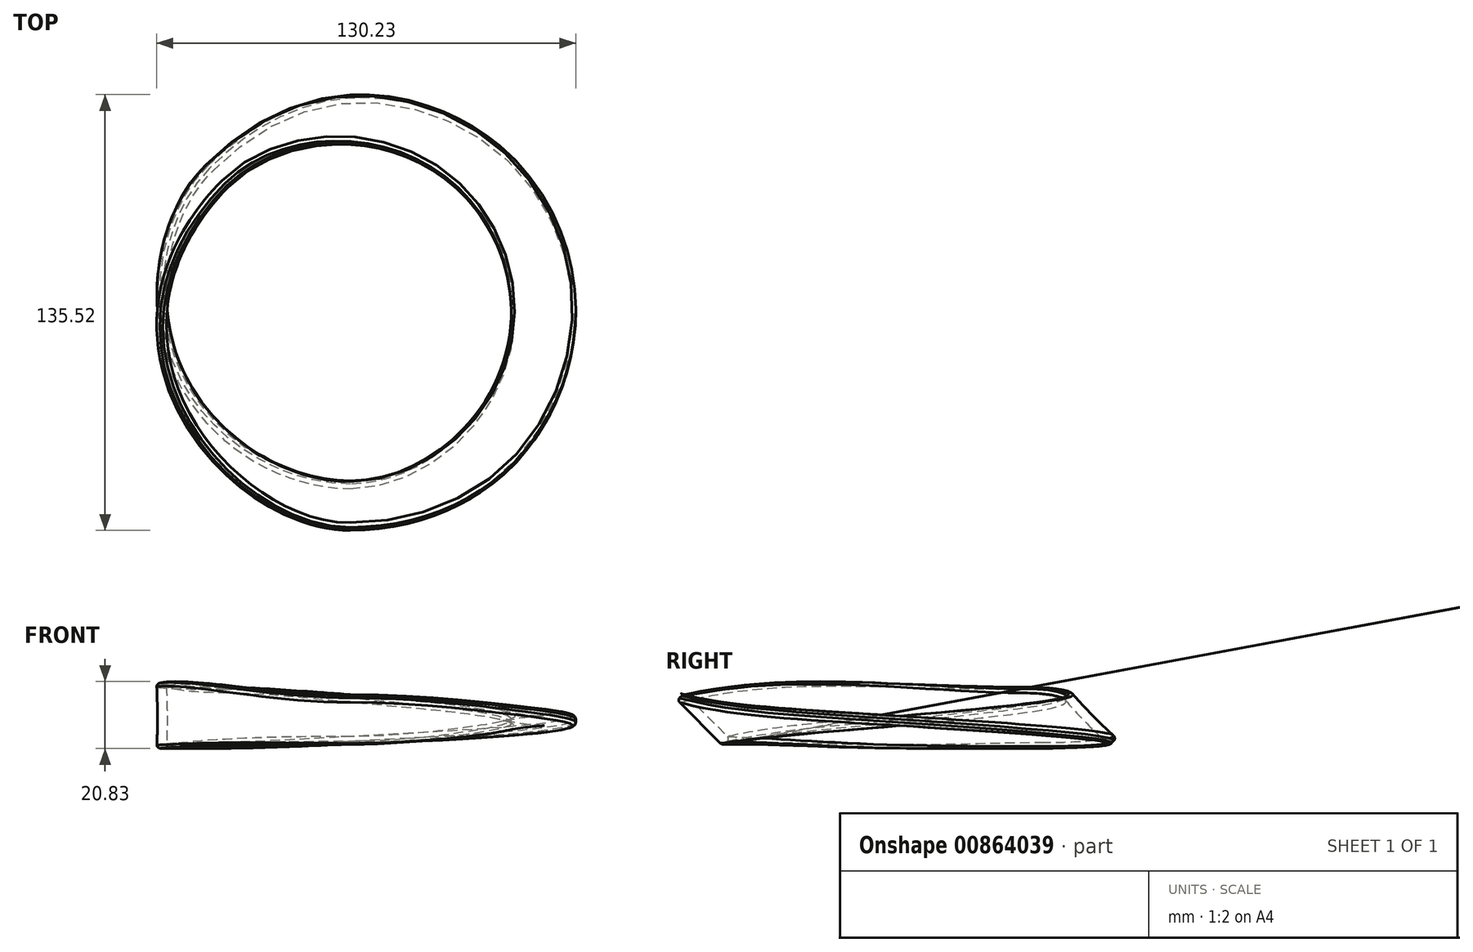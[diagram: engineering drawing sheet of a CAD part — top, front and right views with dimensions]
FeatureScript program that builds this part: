
annotation { "Feature Type Name" : "Feature", "Feature Type Description" : "" }
export const myFeature = defineFeature(function(context is Context, id is Id, definition is map)
    precondition{}
    {
        {
            var Q0;
            Q0=qCreatedBy(makeId("Front.planeOp"),FACE);
            var sketch = newSketch(context, id + "F0", { "sketchPlane" : qUnion([Q0])});
            skLineSegment(sketch, "E0", {"start": v(-60, 10) * mm, "end": v(-60, -10) * mm});
            skLineSegment(sketch, "E1", {"start": v(50, 0) * mm, "end": v(70, 0) * mm});
            skLineSegment(sketch, "E2", {"start": v(0, 0) * mm, "end": v(0, 28.94) * mm, "construction": true});
            skLineSegment(sketch, "E3.0", {"start": v(-57, 10) * mm, "end": v(-57, -10) * mm});
            skLineSegment(sketch, "E4", {"start": v(-60, 10) * mm, "end": v(-57, 10) * mm});
            skLineSegment(sketch, "E5", {"start": v(-60, -10) * mm, "end": v(-57, -10) * mm});
            skLineSegment(sketch, "E6", {"start": v(70, 0) * mm, "end": v(70, -3) * mm});
            skLineSegment(sketch, "E7", {"start": v(70, -3) * mm, "end": v(50, -3) * mm});
            skLineSegment(sketch, "E8", {"start": v(50, -3) * mm, "end": v(50, 0) * mm});
            skSolve(sketch);
        }
        {
            var Q0;
            Q0=sQuery(id+"F0.wireOp",EDGE,"E2");
            var Q1;
            Q1=qCreatedBy(makeId("Front.planeOp"),FACE);
            cPlane(context, id + "F1", {"entities" : qUnion([Q0, Q1]), "cplaneType" : CPlaneType.LINE_ANGLE, "offset" : 25 * mm, "angle" : 45 * degree, "width" : 150 * mm, "height" : 150 * mm});
        }
        {
            var Q0;
            Q0=sQuery(id+"F0.wireOp",EDGE,"E2");
            var Q1;
            Q1=qCreatedBy(makeId("Front.planeOp"),FACE);
            cPlane(context, id + "F2", {"entities" : qUnion([Q0, Q1]), "cplaneType" : CPlaneType.LINE_ANGLE, "offset" : 25 * mm, "angle" : 135 * degree, "width" : 150 * mm, "height" : 150 * mm});
        }
        {
            var Q0;
            Q0=qCreatedBy(id+"F1.planeOp",FACE);
            var sketch = newSketch(context, id + "F3", { "sketchPlane" : qUnion([Q0])});
            skLineSegment(sketch, "E9", {"start": v(60, 0) * mm, "end": v(60, 0) * mm});
            skLineSegment(sketch, "E10", {"start": v(0, 0) * mm, "end": v(-60, 0) * mm, "construction": true});
            skLineSegment(sketch, "E11", {"start": v(61.06, 10.39) * mm, "end": v(53.4, -8.1) * mm});
            skLineSegment(sketch, "E12", {"start": v(-50.76, 3.83) * mm, "end": v(-69.24, -3.83) * mm});
            skLineSegment(sketch, "E13", {"start": v(61.06, 10.39) * mm, "end": v(63.83, 9.24) * mm});
            skLineSegment(sketch, "E14", {"start": v(63.83, 9.24) * mm, "end": v(56.17, -9.24) * mm});
            skLineSegment(sketch, "E15", {"start": v(56.17, -9.24) * mm, "end": v(53.4, -8.1) * mm});
            skLineSegment(sketch, "E16", {"start": v(-50.76, 3.83) * mm, "end": v(-49.61, 1.06) * mm});
            skLineSegment(sketch, "E17", {"start": v(-49.61, 1.06) * mm, "end": v(-68.1, -6.6) * mm});
            skLineSegment(sketch, "E18", {"start": v(-69.24, -3.83) * mm, "end": v(-68.1, -6.6) * mm});
            skSolve(sketch);
        }
        {
            var Q0;
            Q0=qCreatedBy(makeId("Right.planeOp"),FACE);
            var sketch = newSketch(context, id + "F4", { "sketchPlane" : qUnion([Q0])});
            skLineSegment(sketch, "E19", {"start": v(0, 0) * mm, "end": v(-60, 0) * mm, "construction": true});
            skLineSegment(sketch, "E20", {"start": v(0, 0) * mm, "end": v(60, 0) * mm, "construction": true});
            skLineSegment(sketch, "E21", {"start": v(-67.07, 7.07) * mm, "end": v(-52.93, -7.07) * mm});
            skLineSegment(sketch, "E22", {"start": v(52.93, 7.07) * mm, "end": v(67.07, -7.07) * mm});
            skLineSegment(sketch, "E23", {"start": v(-67.07, 7.07) * mm, "end": v(-69.2, 4.95) * mm});
            skLineSegment(sketch, "E24", {"start": v(-69.2, 4.95) * mm, "end": v(-55.05, -9.2) * mm});
            skLineSegment(sketch, "E25", {"start": v(-52.93, -7.07) * mm, "end": v(-55.05, -9.2) * mm});
            skLineSegment(sketch, "E26", {"start": v(52.93, 7.07) * mm, "end": v(50.8, 4.95) * mm});
            skLineSegment(sketch, "E27", {"start": v(50.8, 4.95) * mm, "end": v(64.95, -9.2) * mm});
            skLineSegment(sketch, "E28", {"start": v(67.07, -7.07) * mm, "end": v(64.95, -9.2) * mm});
            skSolve(sketch);
        }
        {
            var Q0;
            Q0=qCreatedBy(id+"F2.planeOp",FACE);
            var sketch = newSketch(context, id + "F5", { "sketchPlane" : qUnion([Q0])});
            skLineSegment(sketch, "E29", {"start": v(0, 0) * mm, "end": v(60, 0) * mm, "construction": true});
            skLineSegment(sketch, "E30", {"start": v(0, 0) * mm, "end": v(-60, 0) * mm, "construction": true});
            skLineSegment(sketch, "E31", {"start": v(69.24, 3.83) * mm, "end": v(50.76, -3.83) * mm});
            skLineSegment(sketch, "E32", {"start": v(-56.17, 9.24) * mm, "end": v(-63.83, -9.24) * mm});
            skLineSegment(sketch, "E33", {"start": v(69.24, 3.83) * mm, "end": v(70.39, 1.06) * mm});
            skLineSegment(sketch, "E34", {"start": v(70.39, 1.06) * mm, "end": v(51.9, -6.6) * mm});
            skLineSegment(sketch, "E35", {"start": v(50.76, -3.83) * mm, "end": v(51.9, -6.6) * mm});
            skLineSegment(sketch, "E36", {"start": v(-56.17, 9.24) * mm, "end": v(-53.4, 8.1) * mm});
            skLineSegment(sketch, "E37", {"start": v(-53.4, 8.1) * mm, "end": v(-61.06, -10.39) * mm});
            skLineSegment(sketch, "E38", {"start": v(-63.83, -9.24) * mm, "end": v(-61.06, -10.39) * mm});
            skSolve(sketch);
        }
        {
            var Q0;
            Q0=makeQuery(id+"F4.imprint","IMPRINT",FACE,{"disambiguationData":[TD([[makeQuery(id+"F4.imprint","IMPRINT",EDGE,{"derivedFrom":sQuery(id+"F4.wireOp",EDGE,"E21")}),-1.0]])]});
            var Q1;
            Q1=makeQuery(id+"F5.imprint","IMPRINT",FACE,{"disambiguationData":[TD([[makeQuery(id+"F5.imprint","IMPRINT",EDGE,{"derivedFrom":sQuery(id+"F5.wireOp",EDGE,"E31")}),1.0]])]});
            var Q2;
            Q2=makeQuery(id+"F0.imprint","IMPRINT",FACE,{"disambiguationData":[TD([[makeQuery(id+"F0.imprint","IMPRINT",EDGE,{"derivedFrom":sQuery(id+"F0.wireOp",EDGE,"E1")}),-1.0]])]});
            var Q3;
            Q3=makeQuery(id+"F3.imprint","IMPRINT",FACE,{"disambiguationData":[TD([[makeQuery(id+"F3.imprint","IMPRINT",EDGE,{"derivedFrom":sQuery(id+"F3.wireOp",EDGE,"E12")}),1.0]])]});
            var Q4;
            Q4=makeQuery(id+"F4.imprint","IMPRINT",FACE,{"disambiguationData":[TD([[makeQuery(id+"F4.imprint","IMPRINT",EDGE,{"derivedFrom":sQuery(id+"F4.wireOp",EDGE,"E22")}),-1.0]])]});
            var Q5;
            Q5=makeQuery(id+"F5.imprint","IMPRINT",FACE,{"disambiguationData":[TD([[makeQuery(id+"F5.imprint","IMPRINT",EDGE,{"derivedFrom":sQuery(id+"F5.wireOp",EDGE,"E32")}),1.0]])]});
            loft(context, id + "F6", {"sheetProfilesArray" : [{ "sheetProfileEntities" : qUnion([Q0]) }, { "sheetProfileEntities" : qUnion([Q1]) }, { "sheetProfileEntities" : qUnion([Q2]) }, { "sheetProfileEntities" : qUnion([Q3]) }, { "sheetProfileEntities" : qUnion([Q4]) }, { "sheetProfileEntities" : qUnion([Q5]) }], "startCondition" : LoftEndDerivativeType.NORMAL_TO_PROFILE, "startMagnitude" : 1, "endCondition" : LoftEndDerivativeType.NORMAL_TO_PROFILE, "endMagnitude" : 1});
        }
        {
            var Q0;
            Q0=makeQuery(id+"F5.imprint","IMPRINT",FACE,{"disambiguationData":[TD([[makeQuery(id+"F5.imprint","IMPRINT",EDGE,{"derivedFrom":sQuery(id+"F5.wireOp",EDGE,"E32")}),1.0]])]});
            var Q1;
            Q1=makeQuery(id+"F0.imprint","IMPRINT",FACE,{"disambiguationData":[TD([[makeQuery(id+"F0.imprint","IMPRINT",EDGE,{"derivedFrom":sQuery(id+"F0.wireOp",EDGE,"E0")}),1.0]])]});
            var Q2;
            Q2=makeQuery(id+"F3.imprint","IMPRINT",FACE,{"disambiguationData":[TD([[makeQuery(id+"F3.imprint","IMPRINT",EDGE,{"derivedFrom":sQuery(id+"F3.wireOp",EDGE,"E11")}),1.0]])]});
            var Q3;
            Q3=makeQuery(id+"F4.imprint","IMPRINT",FACE,{"disambiguationData":[TD([[makeQuery(id+"F4.imprint","IMPRINT",EDGE,{"derivedFrom":sQuery(id+"F4.wireOp",EDGE,"E21")}),-1.0]])]});
            loft(context, id + "F7", {"operationType" : NewBodyOperationType.ADD, "sheetProfilesArray" : [{ "sheetProfileEntities" : qUnion([Q0]) }, { "sheetProfileEntities" : qUnion([Q1]) }, { "sheetProfileEntities" : qUnion([Q2]) }, { "sheetProfileEntities" : qUnion([Q3]) }], "startCondition" : LoftEndDerivativeType.NORMAL_TO_PROFILE, "startMagnitude" : 1, "endCondition" : LoftEndDerivativeType.NORMAL_TO_PROFILE, "endMagnitude" : 1});
        }
        {
            var Q0;
            Q0=makeQuery(id+"F6.opLoft","SWEPT_EDGE",EDGE,{"disambiguationData":[OSD([sQuery(id+"F0.wireOp",EDGE,"E1"),sQuery(id+"F0.wireOp",EDGE,"E3.0"),sQuery(id+"F0.wireOp",EDGE,"E5"),sQuery(id+"F0.wireOp",EDGE,"E8"),sQuery(id+"F3.wireOp",EDGE,"E11"),sQuery(id+"F3.wireOp",EDGE,"E12"),sQuery(id+"F3.wireOp",EDGE,"E15"),sQuery(id+"F3.wireOp",EDGE,"E16"),sQuery(id+"F4.wireOp",EDGE,"E21"),sQuery(id+"F4.wireOp",EDGE,"E22"),sQuery(id+"F4.wireOp",EDGE,"E25"),sQuery(id+"F4.wireOp",EDGE,"E26"),sQuery(id+"F5.wireOp",EDGE,"E31"),sQuery(id+"F5.wireOp",EDGE,"E32"),sQuery(id+"F5.wireOp",EDGE,"E35"),sQuery(id+"F5.wireOp",EDGE,"E36")])]});
            var Q1;
            Q1=makeQuery(id+"F7.opLoft","SWEPT_EDGE",EDGE,{"disambiguationData":[OSD([sQuery(id+"F0.wireOp",EDGE,"E0"),sQuery(id+"F0.wireOp",EDGE,"E5"),sQuery(id+"F5.wireOp",EDGE,"E32"),sQuery(id+"F5.wireOp",EDGE,"E38")])]});
            fillet(context, id + "F8", {"entities" : qUnion([Q0, Q1]), "tangentPropagation" : true, "radius" : 1 * mm, "defaultsChanged" : false, "vertexSettings" : [], "allowEdgeOverflow" : false});
        }
    });
